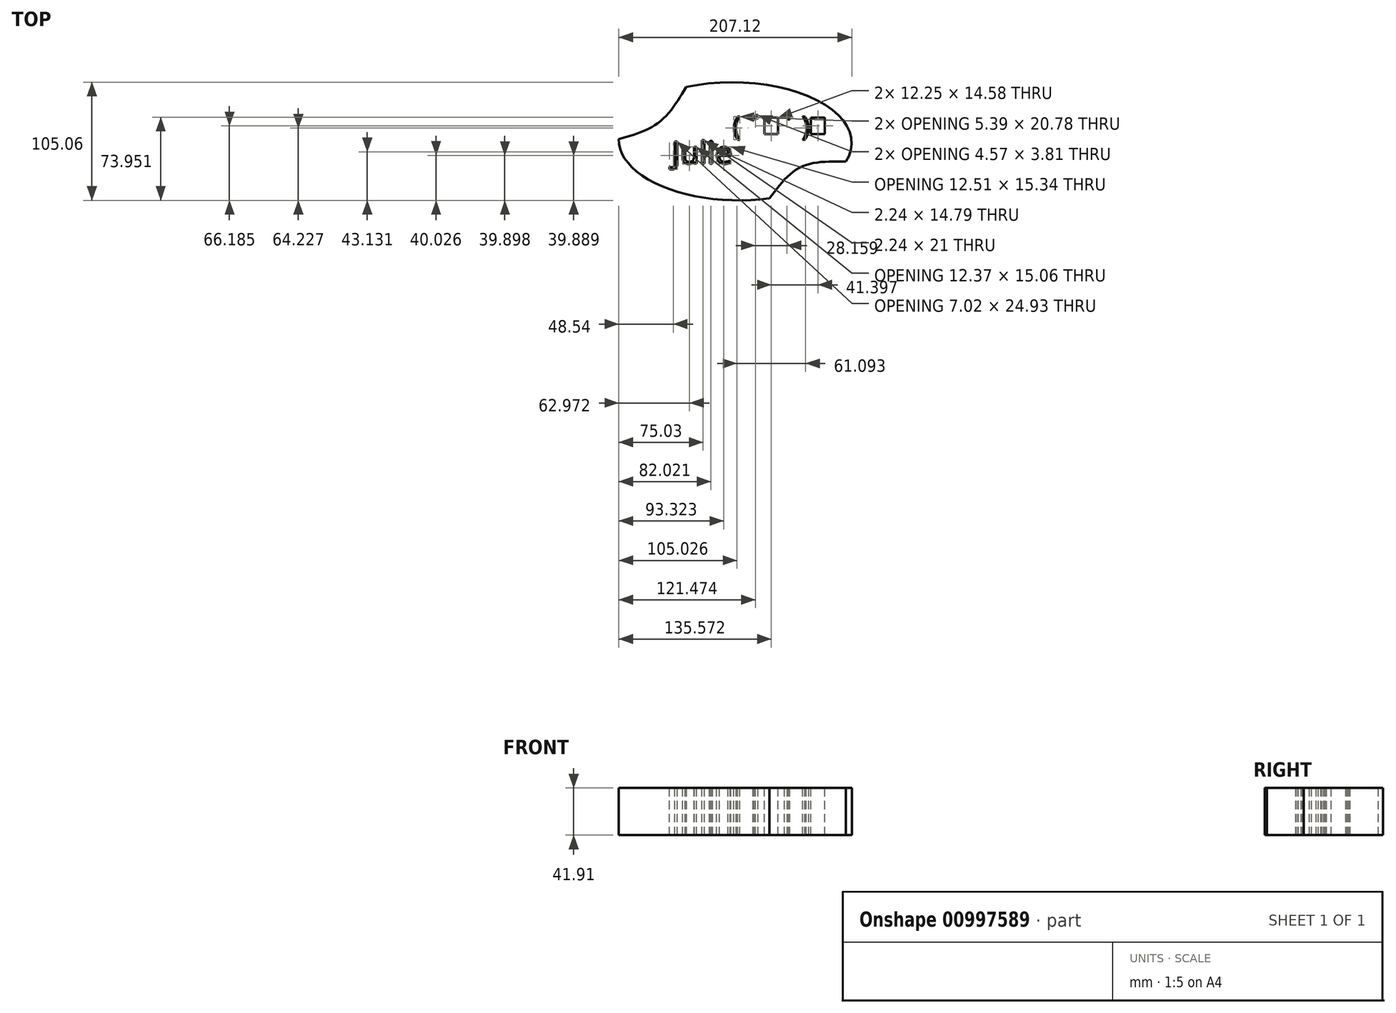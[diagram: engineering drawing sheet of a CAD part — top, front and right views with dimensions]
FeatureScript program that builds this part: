
annotation { "Feature Type Name" : "Feature", "Feature Type Description" : "" }
export const myFeature = defineFeature(function(context is Context, id is Id, definition is map)
    precondition{}
    {
        {
            var Q0;
            Q0=qCreatedBy(makeId("Top.planeOp"),FACE);
            var sketch = newSketch(context, id + "F0", { "sketchPlane" : qUnion([Q0])});
            skEllipticalArc(sketch, "E0", {});
            skFitSpline(sketch, "E1", {"points": [v(-43.66, 48.2) * mm, v(-67.63, 17) * mm, v(-103.56, 1.87) * mm], "startDerivative": vector(-41.88, -69.98) * mm, "endDerivative": vector(-77.99, -22.4) * mm});
            skFitSpline(sketch, "E2", {"points": [v(98.22, -17.98) * mm, v(57.88, -23.16) * mm, v(30.42, -50.6) * mm], "startDerivative": vector(-85.77, 1.1) * mm, "endDerivative": vector(-49.65, -66.48) * mm});
            skEllipticalArc(sketch, "E3.trimOffspring", {});
            const initialGuessF0  = {"E0": [0, 0, -0.9998366326266418, 0.01807506729774145, 0.10357666093475251, 0.052508751383906496, 0, 1.8781194921092725], "E3.trimOffspring": [0, 0, -0.9998366326266418, 0.01807506729774145, 0.10357666093475251, 0.052508751383906496, 2.828003446971442, 5.1567682924865865]};
            skSetInitialGuess(sketch, initialGuessF0);
            skSolve(sketch);
        }
        {
            var Q0;
            Q0=makeQuery(id+"F0.imprint","IMPRINT",FACE,{"disambiguationData":[TD([[makeQuery(id+"F0.imprint","IMPRINT",EDGE,{"derivedFrom":sQuery(id+"F0.wireOp",EDGE,"E0")}),1.0]])]});
            extrude(context, id + "F1", {"entities" : qUnion([Q0]), "depth" : 41.9 * mm, "offsetDistance" : 25.4 * mm});
        }
        {
            var Q0;
            Q0=makeQuery(id+"F1.opExtrude","CAP_FACE",FACE,{"disambiguationData":[OSD([sQuery(id+"F0.wireOp",EDGE,"E0")])],"isStart":false});
            var sketch = newSketch(context, id + "F2", { "sketchPlane" : qUnion([Q0])});
            skText(sketch, "E4", { "text": "Julie", "fontName": "OpenSans-Regular.ttf"});
            const initialGuessF2  = {"E4": [-0.05637, -0.0199, 1, 0, 0.0199]};
            skSetInitialGuess(sketch, initialGuessF2);
            skSolve(sketch);
        }
        {
            var Q0;
            Q0 = qSketchRegion(id + "F2", true);
            extrude(context, id + "F3", {"entities" : qUnion([Q0]), "operationType" : NewBodyOperationType.REMOVE, "oppositeDirection" : true, "depth" : 59.94 * mm, "offsetDistance" : 25.4 * mm});
        }
        {
            var Q0;
            {var subQ0=sQuery(id+"F0.wireOp",EDGE,"E0");Q0=makeQuery(id+"F3.boolean.opBoolean","SPLIT",FACE,{"disambiguationData":[TD([makeQuery(id+"F1.opExtrude","SWEPT_FACE",FACE,{"disambiguationData":[OSD([subQ0])]})])],"derivedFrom":makeQuery(id+"F1.opExtrude","CAP_FACE",FACE,{"disambiguationData":[OSD([subQ0])],"isStart":false})});}
            var sketch = newSketch(context, id + "F4", { "sketchPlane" : qUnion([Q0])});
            skText(sketch, "E5", { "text": "( ´▽` )ﾉ", "fontName": "OpenSans-Regular.ttf"});
            const initialGuessF4  = {"E5": [-0.00218, 0.00508, 1, 0, 0.01715]};
            skSetInitialGuess(sketch, initialGuessF4);
            skSolve(sketch);
        }
        {
            var Q0;
            Q0 = qSketchRegion(id + "F4", true);
            extrude(context, id + "F5", {"entities" : qUnion([Q0]), "operationType" : NewBodyOperationType.REMOVE, "oppositeDirection" : true, "depth" : 63.25 * mm, "offsetDistance" : 25.4 * mm});
        }
    });
